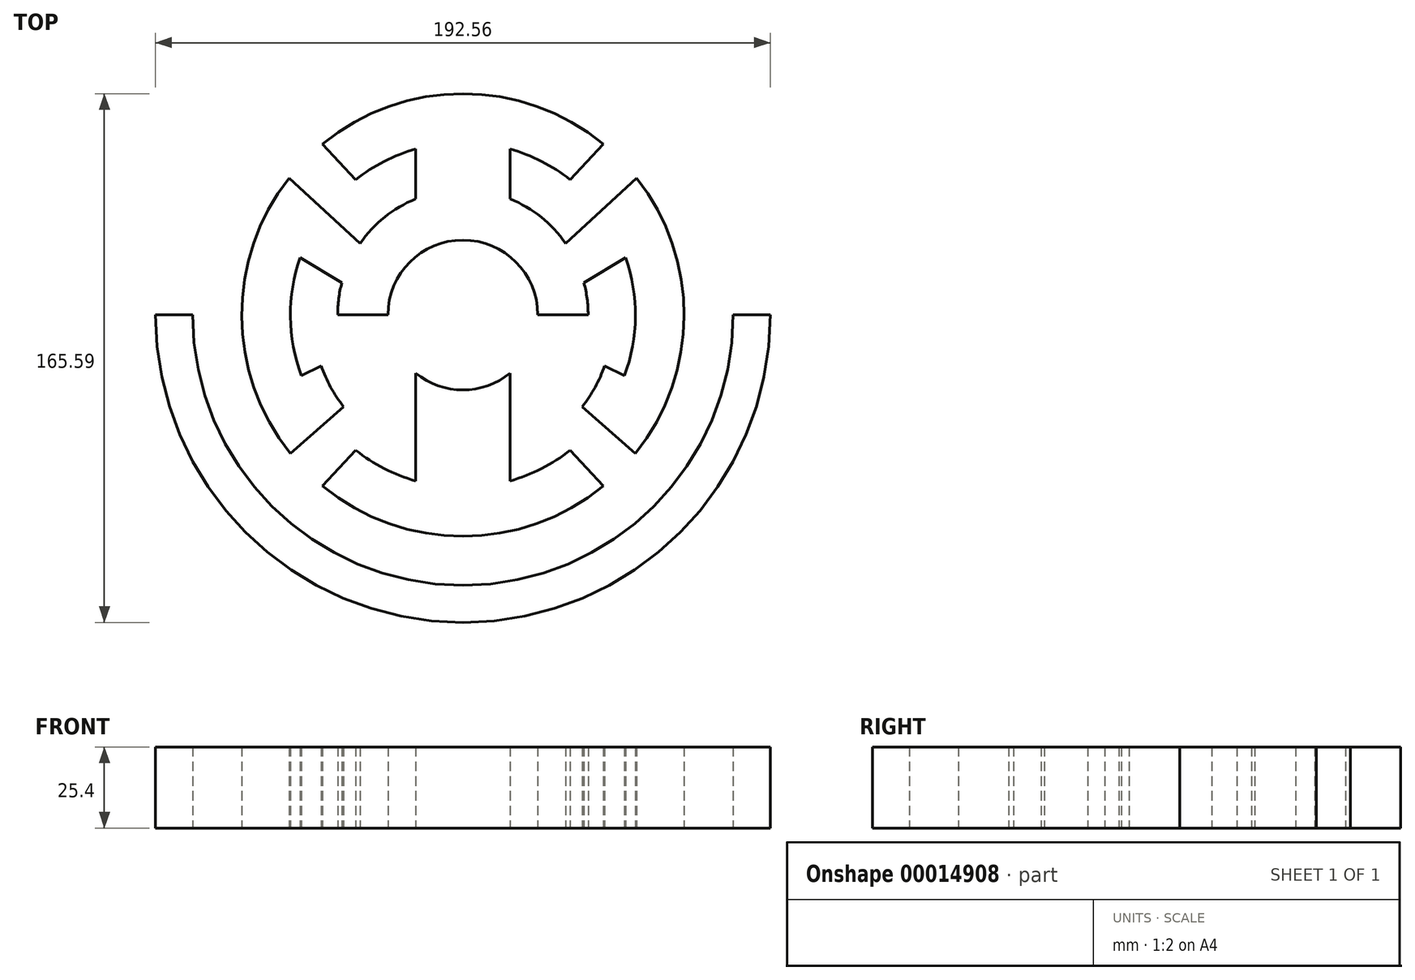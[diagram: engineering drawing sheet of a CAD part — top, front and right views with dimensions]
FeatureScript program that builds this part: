
annotation { "Feature Type Name" : "Feature", "Feature Type Description" : "" }
export const myFeature = defineFeature(function(context is Context, id is Id, definition is map)
    precondition{}
    {
        {
            var Q0;
            Q0=qCreatedBy(makeId("Top.planeOp"),FACE);
            var sketch = newSketch(context, id + "F0", { "sketchPlane" : qUnion([Q0])});
            skCircle(sketch, "E0", {"center": v(0, 0) * mm, "radius": 96.28 * mm});
            skCircle(sketch, "E1", {"center": v(0, 0) * mm, "radius": 84.65 * mm});
            skCircle(sketch, "E2", {"center": v(0, 0) * mm, "radius": 23.48 * mm});
            skCircle(sketch, "E3", {"center": v(0, 0) * mm, "radius": 39.24 * mm});
            skCircle(sketch, "E4", {"center": v(0, 0) * mm, "radius": 69.3 * mm});
            skCircle(sketch, "E5", {"center": v(0, 0) * mm, "radius": 54.05 * mm});
            skLineSegment(sketch, "E6", {"start": v(14.83, 67.7) * mm, "end": v(14.83, -51.98) * mm});
            skLineSegment(sketch, "E7", {"start": v(0, 69.3) * mm, "end": v(0, -96.28) * mm});
            skLineSegment(sketch, "E8.MirrorCS", {"start": v(-14.83, 67.7) * mm, "end": v(-14.83, -51.98) * mm});
            skLineSegment(sketch, "E9", {"start": v(96.28, 0) * mm, "end": v(-96.28, 0) * mm});
            skLineSegment(sketch, "E10", {"start": v(33.56, -42.37) * mm, "end": v(44.04, -53.52) * mm});
            skLineSegment(sketch, "E11.MirrorCS", {"start": v(-33.56, -42.37) * mm, "end": v(-44.04, -53.52) * mm});
            skLineSegment(sketch, "E12.MirrorCS", {"start": v(33.56, 42.37) * mm, "end": v(44.04, 53.52) * mm});
            skLineSegment(sketch, "E13.MirrorCS", {"start": v(-33.56, 42.37) * mm, "end": v(-44.04, 53.52) * mm});
            skCircle(sketch, "E14", {"center": v(0, 0) * mm, "radius": 47.19 * mm});
            skLineSegment(sketch, "E15", {"start": v(32.19, 22.45) * mm, "end": v(54.44, 42.9) * mm});
            skLineSegment(sketch, "E16", {"start": v(54.08, -43.34) * mm, "end": v(37.38, -28.8) * mm});
            skLineSegment(sketch, "E17", {"start": v(64.28, -25.92) * mm, "end": v(44.43, -15.9) * mm});
            skLineSegment(sketch, "E18", {"start": v(37.92, 10.11) * mm, "end": v(64.25, 25.99) * mm});
            skLineSegment(sketch, "E19.MirrorCS", {"start": v(-32.19, 22.45) * mm, "end": v(-54.44, 42.9) * mm});
            skLineSegment(sketch, "E20.MirrorCS", {"start": v(-37.92, 10.11) * mm, "end": v(-64.25, 25.99) * mm});
            skLineSegment(sketch, "E21.MirrorCS", {"start": v(-64.28, -25.92) * mm, "end": v(-44.43, -15.9) * mm});
            skLineSegment(sketch, "E22.MirrorCS", {"start": v(-54.08, -43.34) * mm, "end": v(-37.38, -28.8) * mm});
            skSolve(sketch);
        }
        {
            var Q0;
            {var subQ3=sQuery(id+"F0.wireOp",EDGE,"E3");var subQ5=sQuery(id+"F0.wireOp",EDGE,"E15");var subQ7=makeQuery(id+"F0.imprint","INTERSECT",VERTEX,{"derivedFrom":[subQ3,subQ5]});Q0=makeQuery(id+"F0.imprint","IMPRINT",FACE,{"disambiguationData":[TD([[makeQuery(id+"F0.imprint","IMPRINT",EDGE,{"disambiguationData":[TD([[subQ7,1.0]])],"derivedFrom":subQ3}),-1.0]])]});}
            var Q1;
            {var subQ3=sQuery(id+"F0.wireOp",EDGE,"E2");var subQ5=sQuery(id+"F0.wireOp",EDGE,"E6");var subQ7=makeQuery(id+"F0.imprint","INTERSECT",VERTEX,{"disambiguationData":[OD(0.0)],"derivedFrom":[subQ3,subQ5]});Q1=makeQuery(id+"F0.imprint","IMPRINT",FACE,{"disambiguationData":[TD([[makeQuery(id+"F0.imprint","IMPRINT",EDGE,{"disambiguationData":[TD([[subQ7,-1.0]])],"derivedFrom":subQ3}),-1.0]])]});}
            var Q2;
            {var subQ3=sQuery(id+"F0.wireOp",EDGE,"E4");var subQ5=sQuery(id+"F0.wireOp",EDGE,"E6");var subQ7=makeQuery(id+"F0.imprint","INTERSECT",VERTEX,{"derivedFrom":[subQ3,subQ5]});Q2=makeQuery(id+"F0.imprint","IMPRINT",FACE,{"disambiguationData":[TD([[makeQuery(id+"F0.imprint","IMPRINT",EDGE,{"disambiguationData":[TD([[subQ7,-1.0]])],"derivedFrom":subQ3}),1.0]])]});}
            var Q3;
            {var subQ0=sQuery(id+"F0.wireOp",EDGE,"E18");var subQ3=sQuery(id+"F0.wireOp",EDGE,"E4");var subQ4=makeQuery(id+"F0.imprint","INTERSECT",VERTEX,{"derivedFrom":[subQ3,subQ0]});Q3=makeQuery(id+"F0.imprint","IMPRINT",FACE,{"disambiguationData":[TD([[makeQuery(id+"F0.imprint","IMPRINT",EDGE,{"disambiguationData":[TD([[subQ4,1.0]])],"derivedFrom":subQ3}),1.0]])]});}
            var Q4;
            {var subQ0=sQuery(id+"F0.wireOp",EDGE,"E11.MirrorCS");Q4=makeQuery(id+"F0.imprint","IMPRINT",FACE,{"disambiguationData":[TD([[makeQuery(id+"F0.imprint","IMPRINT",EDGE,{"derivedFrom":subQ0}),1.0]])]});}
            var Q5;
            {var subQ3=sQuery(id+"F0.wireOp",EDGE,"E7");var subQ5=sQuery(id+"F0.wireOp",EDGE,"E5");var subQ7=makeQuery(id+"F0.imprint","INTERSECT",VERTEX,{"disambiguationData":[OD(0.0)],"derivedFrom":[subQ5,subQ3]});Q5=makeQuery(id+"F0.imprint","IMPRINT",FACE,{"disambiguationData":[TD([[makeQuery(id+"F0.imprint","IMPRINT",EDGE,{"disambiguationData":[TD([[subQ7,-1.0]])],"derivedFrom":subQ5}),1.0]])]});}
            var Q6;
            {var subQ3=sQuery(id+"F0.wireOp",EDGE,"E2");var subQ5=sQuery(id+"F0.wireOp",EDGE,"E7");var subQ7=makeQuery(id+"F0.imprint","INTERSECT",VERTEX,{"disambiguationData":[OD(1.0)],"derivedFrom":[subQ3,subQ5]});Q6=makeQuery(id+"F0.imprint","IMPRINT",FACE,{"disambiguationData":[TD([[makeQuery(id+"F0.imprint","IMPRINT",EDGE,{"disambiguationData":[TD([[subQ7,-1.0]])],"derivedFrom":subQ3}),-1.0]])]});}
            var Q7;
            {var subQ0=sQuery(id+"F0.wireOp",EDGE,"E8.MirrorCS");var subQ3=sQuery(id+"F0.wireOp",EDGE,"E2");var subQ4=makeQuery(id+"F0.imprint","INTERSECT",VERTEX,{"disambiguationData":[OD(1.0)],"derivedFrom":[subQ3,subQ0]});Q7=makeQuery(id+"F0.imprint","IMPRINT",FACE,{"disambiguationData":[TD([[makeQuery(id+"F0.imprint","IMPRINT",EDGE,{"disambiguationData":[TD([[subQ4,-1.0]])],"derivedFrom":subQ3}),-1.0]])]});}
            var Q8;
            {var subQ0=sQuery(id+"F0.wireOp",EDGE,"E12.MirrorCS");Q8=makeQuery(id+"F0.imprint","IMPRINT",FACE,{"disambiguationData":[TD([[makeQuery(id+"F0.imprint","IMPRINT",EDGE,{"derivedFrom":subQ0}),1.0]])]});}
            var Q9;
            {var subQ3=sQuery(id+"F0.wireOp",EDGE,"E4");var subQ5=sQuery(id+"F0.wireOp",EDGE,"E7");var subQ7=makeQuery(id+"F0.imprint","INTERSECT",VERTEX,{"disambiguationData":[OD(0.0)],"derivedFrom":[subQ3,subQ5]});Q9=makeQuery(id+"F0.imprint","IMPRINT",FACE,{"disambiguationData":[TD([[makeQuery(id+"F0.imprint","IMPRINT",EDGE,{"disambiguationData":[TD([[subQ7,-1.0]])],"derivedFrom":subQ3}),1.0]])]});}
            var Q10;
            {var subQ3=sQuery(id+"F0.wireOp",EDGE,"E4");var subQ5=sQuery(id+"F0.wireOp",EDGE,"E16");var subQ7=makeQuery(id+"F0.imprint","INTERSECT",VERTEX,{"derivedFrom":[subQ3,subQ5]});Q10=makeQuery(id+"F0.imprint","IMPRINT",FACE,{"disambiguationData":[TD([[makeQuery(id+"F0.imprint","IMPRINT",EDGE,{"disambiguationData":[TD([[subQ7,-1.0]])],"derivedFrom":subQ3}),1.0]])]});}
            var Q11;
            {var subQ0=sQuery(id+"F0.wireOp",EDGE,"E17");var subQ3=sQuery(id+"F0.wireOp",EDGE,"E4");var subQ4=makeQuery(id+"F0.imprint","INTERSECT",VERTEX,{"derivedFrom":[subQ3,subQ0]});Q11=makeQuery(id+"F0.imprint","IMPRINT",FACE,{"disambiguationData":[TD([[makeQuery(id+"F0.imprint","IMPRINT",EDGE,{"disambiguationData":[TD([[subQ4,-1.0]])],"derivedFrom":subQ3}),1.0]])]});}
            var Q12;
            {var subQ3=sQuery(id+"F0.wireOp",EDGE,"E0");var subQ5=sQuery(id+"F0.wireOp",EDGE,"E7");var subQ7=makeQuery(id+"F0.imprint","INTERSECT",VERTEX,{"derivedFrom":[subQ3,subQ5]});Q12=makeQuery(id+"F0.imprint","IMPRINT",FACE,{"disambiguationData":[TD([[makeQuery(id+"F0.imprint","IMPRINT",EDGE,{"disambiguationData":[TD([[subQ7,-1.0]])],"derivedFrom":subQ3}),1.0]])]});}
            var Q13;
            {var subQ0=sQuery(id+"F0.wireOp",EDGE,"E20.MirrorCS");var subQ3=sQuery(id+"F0.wireOp",EDGE,"E4");var subQ4=makeQuery(id+"F0.imprint","INTERSECT",VERTEX,{"derivedFrom":[subQ3,subQ0]});Q13=makeQuery(id+"F0.imprint","IMPRINT",FACE,{"disambiguationData":[TD([[makeQuery(id+"F0.imprint","IMPRINT",EDGE,{"disambiguationData":[TD([[subQ4,-1.0]])],"derivedFrom":subQ3}),1.0]])]});}
            var Q14;
            {var subQ3=sQuery(id+"F0.wireOp",EDGE,"E4");var subQ5=sQuery(id+"F0.wireOp",EDGE,"E21.MirrorCS");var subQ7=makeQuery(id+"F0.imprint","INTERSECT",VERTEX,{"derivedFrom":[subQ3,subQ5]});Q14=makeQuery(id+"F0.imprint","IMPRINT",FACE,{"disambiguationData":[TD([[makeQuery(id+"F0.imprint","IMPRINT",EDGE,{"disambiguationData":[TD([[subQ7,-1.0]])],"derivedFrom":subQ3}),1.0]])]});}
            var Q15;
            {var subQ3=sQuery(id+"F0.wireOp",EDGE,"E0");var subQ5=sQuery(id+"F0.wireOp",EDGE,"E7");var subQ7=makeQuery(id+"F0.imprint","INTERSECT",VERTEX,{"derivedFrom":[subQ3,subQ5]});Q15=makeQuery(id+"F0.imprint","IMPRINT",FACE,{"disambiguationData":[TD([[makeQuery(id+"F0.imprint","IMPRINT",EDGE,{"disambiguationData":[TD([[subQ7,1.0]])],"derivedFrom":subQ3}),1.0]])]});}
            var Q16;
            {var subQ1=sQuery(id+"F0.wireOp",EDGE,"E5");var subQ5=sQuery(id+"F0.wireOp",EDGE,"E16");var subQ6=makeQuery(id+"F0.imprint","INTERSECT",VERTEX,{"derivedFrom":[subQ1,subQ5]});Q16=makeQuery(id+"F0.imprint","IMPRINT",FACE,{"disambiguationData":[TD([[makeQuery(id+"F0.imprint","IMPRINT",EDGE,{"disambiguationData":[TD([[subQ6,-1.0]])],"derivedFrom":subQ1}),1.0]])]});}
            var Q17;
            {var subQ3=sQuery(id+"F0.wireOp",EDGE,"E4");var subQ5=sQuery(id+"F0.wireOp",EDGE,"E15");var subQ7=makeQuery(id+"F0.imprint","INTERSECT",VERTEX,{"derivedFrom":[subQ3,subQ5]});Q17=makeQuery(id+"F0.imprint","IMPRINT",FACE,{"disambiguationData":[TD([[makeQuery(id+"F0.imprint","IMPRINT",EDGE,{"disambiguationData":[TD([[subQ7,1.0]])],"derivedFrom":subQ3}),1.0]])]});}
            var Q18;
            {var subQ3=sQuery(id+"F0.wireOp",EDGE,"E7");var subQ5=sQuery(id+"F0.wireOp",EDGE,"E3");var subQ7=makeQuery(id+"F0.imprint","INTERSECT",VERTEX,{"disambiguationData":[OD(0.0)],"derivedFrom":[subQ5,subQ3]});Q18=makeQuery(id+"F0.imprint","IMPRINT",FACE,{"disambiguationData":[TD([[makeQuery(id+"F0.imprint","IMPRINT",EDGE,{"disambiguationData":[TD([[subQ7,-1.0]])],"derivedFrom":subQ5}),-1.0]])]});}
            var Q19;
            {var subQ0=sQuery(id+"F0.wireOp",EDGE,"E19.MirrorCS");var subQ3=sQuery(id+"F0.wireOp",EDGE,"E4");var subQ4=makeQuery(id+"F0.imprint","INTERSECT",VERTEX,{"derivedFrom":[subQ3,subQ0]});Q19=makeQuery(id+"F0.imprint","IMPRINT",FACE,{"disambiguationData":[TD([[makeQuery(id+"F0.imprint","IMPRINT",EDGE,{"disambiguationData":[TD([[subQ4,-1.0]])],"derivedFrom":subQ3}),1.0]])]});}
            var Q20;
            {var subQ1=sQuery(id+"F0.wireOp",EDGE,"E8.MirrorCS");var subQ5=sQuery(id+"F0.wireOp",EDGE,"E5");var subQ6=makeQuery(id+"F0.imprint","INTERSECT",VERTEX,{"disambiguationData":[OD(0.0)],"derivedFrom":[subQ5,subQ1]});Q20=makeQuery(id+"F0.imprint","IMPRINT",FACE,{"disambiguationData":[TD([[makeQuery(id+"F0.imprint","IMPRINT",EDGE,{"disambiguationData":[TD([[subQ6,-1.0]])],"derivedFrom":subQ5}),1.0]])]});}
            var Q21;
            {var subQ0=sQuery(id+"F0.wireOp",EDGE,"E21.MirrorCS");var subQ3=sQuery(id+"F0.wireOp",EDGE,"E4");var subQ4=makeQuery(id+"F0.imprint","INTERSECT",VERTEX,{"derivedFrom":[subQ3,subQ0]});Q21=makeQuery(id+"F0.imprint","IMPRINT",FACE,{"disambiguationData":[TD([[makeQuery(id+"F0.imprint","IMPRINT",EDGE,{"disambiguationData":[TD([[subQ4,1.0]])],"derivedFrom":subQ3}),1.0]])]});}
            var Q22;
            {var subQ0=sQuery(id+"F0.wireOp",EDGE,"E9");var subQ3=sQuery(id+"F0.wireOp",EDGE,"E2");var subQ4=makeQuery(id+"F0.imprint","INTERSECT",VERTEX,{"disambiguationData":[OD(1.0)],"derivedFrom":[subQ3,subQ0]});Q22=makeQuery(id+"F0.imprint","IMPRINT",FACE,{"disambiguationData":[TD([[makeQuery(id+"F0.imprint","IMPRINT",EDGE,{"disambiguationData":[TD([[subQ4,-1.0]])],"derivedFrom":subQ3}),-1.0]])]});}
            var Q23;
            {var subQ1=sQuery(id+"F0.wireOp",EDGE,"E8.MirrorCS");var subQ5=sQuery(id+"F0.wireOp",EDGE,"E3");var subQ6=makeQuery(id+"F0.imprint","INTERSECT",VERTEX,{"disambiguationData":[OD(1.0)],"derivedFrom":[subQ5,subQ1]});Q23=makeQuery(id+"F0.imprint","IMPRINT",FACE,{"disambiguationData":[TD([[makeQuery(id+"F0.imprint","IMPRINT",EDGE,{"disambiguationData":[TD([[subQ6,-1.0]])],"derivedFrom":subQ5}),-1.0]])]});}
            var Q24;
            {var subQ0=sQuery(id+"F0.wireOp",EDGE,"E6");var subQ3=sQuery(id+"F0.wireOp",EDGE,"E2");var subQ4=makeQuery(id+"F0.imprint","INTERSECT",VERTEX,{"disambiguationData":[OD(0.0)],"derivedFrom":[subQ3,subQ0]});Q24=makeQuery(id+"F0.imprint","IMPRINT",FACE,{"disambiguationData":[TD([[makeQuery(id+"F0.imprint","IMPRINT",EDGE,{"disambiguationData":[TD([[subQ4,1.0]])],"derivedFrom":subQ3}),-1.0]])]});}
            var Q25;
            {var subQ3=sQuery(id+"F0.wireOp",EDGE,"E6");var subQ5=sQuery(id+"F0.wireOp",EDGE,"E5");var subQ7=makeQuery(id+"F0.imprint","INTERSECT",VERTEX,{"disambiguationData":[OD(1.0)],"derivedFrom":[subQ5,subQ3]});Q25=makeQuery(id+"F0.imprint","IMPRINT",FACE,{"disambiguationData":[TD([[makeQuery(id+"F0.imprint","IMPRINT",EDGE,{"disambiguationData":[TD([[subQ7,-1.0]])],"derivedFrom":subQ5}),1.0]])]});}
            var Q26;
            {var subQ0=sQuery(id+"F0.wireOp",EDGE,"E18");var subQ3=sQuery(id+"F0.wireOp",EDGE,"E5");var subQ4=makeQuery(id+"F0.imprint","INTERSECT",VERTEX,{"derivedFrom":[subQ3,subQ0]});Q26=makeQuery(id+"F0.imprint","IMPRINT",FACE,{"disambiguationData":[TD([[makeQuery(id+"F0.imprint","IMPRINT",EDGE,{"disambiguationData":[TD([[subQ4,-1.0]])],"derivedFrom":subQ3}),1.0]])]});}
            var Q27;
            {var subQ0=sQuery(id+"F0.wireOp",EDGE,"E9");var subQ3=sQuery(id+"F0.wireOp",EDGE,"E0");var subQ6=makeQuery(id+"F0.imprint","INTERSECT",VERTEX,{"disambiguationData":[OD(0.0)],"derivedFrom":[subQ3,subQ0]});Q27=makeQuery(id+"F0.imprint","IMPRINT",FACE,{"disambiguationData":[TD([[makeQuery(id+"F0.imprint","IMPRINT",EDGE,{"disambiguationData":[TD([[subQ6,-1.0]])],"derivedFrom":subQ3}),1.0]])]});}
            var Q28;
            {var subQ0=sQuery(id+"F0.wireOp",EDGE,"E9");var subQ3=sQuery(id+"F0.wireOp",EDGE,"E2");var subQ4=makeQuery(id+"F0.imprint","INTERSECT",VERTEX,{"disambiguationData":[OD(0.0)],"derivedFrom":[subQ3,subQ0]});Q28=makeQuery(id+"F0.imprint","IMPRINT",FACE,{"disambiguationData":[TD([[makeQuery(id+"F0.imprint","IMPRINT",EDGE,{"disambiguationData":[TD([[subQ4,1.0]])],"derivedFrom":subQ3}),-1.0]])]});}
            var Q29;
            {var subQ1=sQuery(id+"F0.wireOp",EDGE,"E5");var subQ5=sQuery(id+"F0.wireOp",EDGE,"E21.MirrorCS");var subQ6=makeQuery(id+"F0.imprint","INTERSECT",VERTEX,{"derivedFrom":[subQ1,subQ5]});Q29=makeQuery(id+"F0.imprint","IMPRINT",FACE,{"disambiguationData":[TD([[makeQuery(id+"F0.imprint","IMPRINT",EDGE,{"disambiguationData":[TD([[subQ6,-1.0]])],"derivedFrom":subQ1}),1.0]])]});}
            var Q30;
            {var subQ3=sQuery(id+"F0.wireOp",EDGE,"E5");var subQ5=sQuery(id+"F0.wireOp",EDGE,"E19.MirrorCS");var subQ7=makeQuery(id+"F0.imprint","INTERSECT",VERTEX,{"derivedFrom":[subQ3,subQ5]});Q30=makeQuery(id+"F0.imprint","IMPRINT",FACE,{"disambiguationData":[TD([[makeQuery(id+"F0.imprint","IMPRINT",EDGE,{"disambiguationData":[TD([[subQ7,-1.0]])],"derivedFrom":subQ3}),1.0]])]});}
            var Q31;
            {var subQ3=sQuery(id+"F0.wireOp",EDGE,"E2");var subQ5=sQuery(id+"F0.wireOp",EDGE,"E8.MirrorCS");var subQ7=makeQuery(id+"F0.imprint","INTERSECT",VERTEX,{"disambiguationData":[OD(0.0)],"derivedFrom":[subQ3,subQ5]});Q31=makeQuery(id+"F0.imprint","IMPRINT",FACE,{"disambiguationData":[TD([[makeQuery(id+"F0.imprint","IMPRINT",EDGE,{"disambiguationData":[TD([[subQ7,-1.0]])],"derivedFrom":subQ3}),-1.0]])]});}
            var Q32;
            {var subQ1=sQuery(id+"F0.wireOp",EDGE,"E7");var subQ5=sQuery(id+"F0.wireOp",EDGE,"E3");var subQ6=makeQuery(id+"F0.imprint","INTERSECT",VERTEX,{"disambiguationData":[OD(1.0)],"derivedFrom":[subQ5,subQ1]});Q32=makeQuery(id+"F0.imprint","IMPRINT",FACE,{"disambiguationData":[TD([[makeQuery(id+"F0.imprint","IMPRINT",EDGE,{"disambiguationData":[TD([[subQ6,-1.0]])],"derivedFrom":subQ5}),-1.0]])]});}
            var Q33;
            {var subQ3=sQuery(id+"F0.wireOp",EDGE,"E6");var subQ5=sQuery(id+"F0.wireOp",EDGE,"E3");var subQ7=makeQuery(id+"F0.imprint","INTERSECT",VERTEX,{"disambiguationData":[OD(0.0)],"derivedFrom":[subQ5,subQ3]});Q33=makeQuery(id+"F0.imprint","IMPRINT",FACE,{"disambiguationData":[TD([[makeQuery(id+"F0.imprint","IMPRINT",EDGE,{"disambiguationData":[TD([[subQ7,-1.0]])],"derivedFrom":subQ5}),-1.0]])]});}
            var Q34;
            {var subQ3=sQuery(id+"F0.wireOp",EDGE,"E3");var subQ5=sQuery(id+"F0.wireOp",EDGE,"E19.MirrorCS");var subQ7=makeQuery(id+"F0.imprint","INTERSECT",VERTEX,{"derivedFrom":[subQ3,subQ5]});Q34=makeQuery(id+"F0.imprint","IMPRINT",FACE,{"disambiguationData":[TD([[makeQuery(id+"F0.imprint","IMPRINT",EDGE,{"disambiguationData":[TD([[subQ7,-1.0]])],"derivedFrom":subQ3}),-1.0]])]});}
            var Q35;
            {var subQ3=sQuery(id+"F0.wireOp",EDGE,"E6");var subQ5=sQuery(id+"F0.wireOp",EDGE,"E5");var subQ7=makeQuery(id+"F0.imprint","INTERSECT",VERTEX,{"disambiguationData":[OD(0.0)],"derivedFrom":[subQ5,subQ3]});Q35=makeQuery(id+"F0.imprint","IMPRINT",FACE,{"disambiguationData":[TD([[makeQuery(id+"F0.imprint","IMPRINT",EDGE,{"disambiguationData":[TD([[subQ7,1.0]])],"derivedFrom":subQ5}),1.0]])]});}
            var Q36;
            {var subQ0=sQuery(id+"F0.wireOp",EDGE,"E10");Q36=makeQuery(id+"F0.imprint","IMPRINT",FACE,{"disambiguationData":[TD([[makeQuery(id+"F0.imprint","IMPRINT",EDGE,{"derivedFrom":subQ0}),-1.0]])]});}
            var Q37;
            {var subQ3=sQuery(id+"F0.wireOp",EDGE,"E2");var subQ5=sQuery(id+"F0.wireOp",EDGE,"E7");var subQ7=makeQuery(id+"F0.imprint","INTERSECT",VERTEX,{"disambiguationData":[OD(0.0)],"derivedFrom":[subQ3,subQ5]});Q37=makeQuery(id+"F0.imprint","IMPRINT",FACE,{"disambiguationData":[TD([[makeQuery(id+"F0.imprint","IMPRINT",EDGE,{"disambiguationData":[TD([[subQ7,-1.0]])],"derivedFrom":subQ3}),-1.0]])]});}
            var Q38;
            {var subQ0=sQuery(id+"F0.wireOp",EDGE,"E13.MirrorCS");Q38=makeQuery(id+"F0.imprint","IMPRINT",FACE,{"disambiguationData":[TD([[makeQuery(id+"F0.imprint","IMPRINT",EDGE,{"derivedFrom":subQ0}),-1.0]])]});}
            extrude(context, id + "F1", {"entities" : qUnion([Q0, Q1, Q2, Q3, Q4, Q5, Q6, Q7, Q8, Q9, Q10, Q11, Q12, Q13, Q14, Q15, Q16, Q17, Q18, Q19, Q20, Q21, Q22, Q23, Q24, Q25, Q26, Q27, Q28, Q29, Q30, Q31, Q32, Q33, Q34, Q35, Q36, Q37, Q38]), "depth" : 25.4 * mm});
        }
    });
